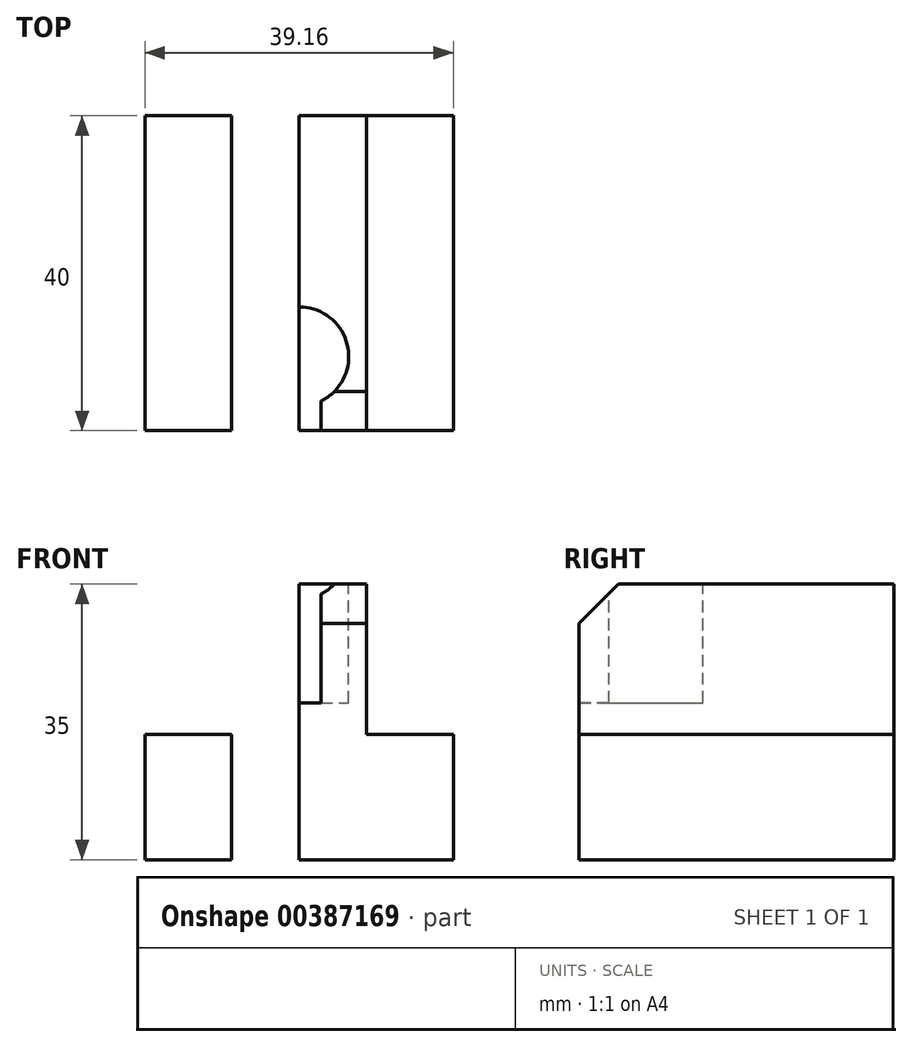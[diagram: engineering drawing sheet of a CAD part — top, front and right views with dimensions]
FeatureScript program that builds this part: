
annotation { "Feature Type Name" : "Feature", "Feature Type Description" : "" }
export const myFeature = defineFeature(function(context is Context, id is Id, definition is map)
    precondition{}
    {
        {
            var Q0;
            Q0=qCreatedBy(makeId("Front.planeOp"),FACE);
            var sketch = newSketch(context, id + "F0", { "sketchPlane" : qUnion([Q0])});
            skLineSegment(sketch, "E0", {"start": v(0, 0) * mm, "end": v(19.58, 0) * mm});
            skLineSegment(sketch, "E1", {"start": v(0, 0) * mm, "end": v(-19.58, 0) * mm});
            skLineSegment(sketch, "E2", {"start": v(0, 0) * mm, "end": v(0, 35) * mm});
            skLineSegment(sketch, "E3", {"start": v(19.58, 0) * mm, "end": v(8.59, 0) * mm});
            skLineSegment(sketch, "E4.MirrorCS", {"start": v(-19.58, 0) * mm, "end": v(-8.59, 0) * mm});
            skLineSegment(sketch, "E5", {"start": v(8.59, 0) * mm, "end": v(8.59, 35) * mm});
            skLineSegment(sketch, "E6", {"start": v(8.59, 35) * mm, "end": v(0, 35) * mm});
            skLineSegment(sketch, "E7.MirrorCS", {"start": v(-8.59, 35) * mm, "end": v(0, 35) * mm});
            skLineSegment(sketch, "E8.MirrorCS", {"start": v(-8.59, 0) * mm, "end": v(-8.59, 35) * mm});
            skLineSegment(sketch, "E9", {"start": v(0, 35) * mm, "end": v(0, 19.94) * mm});
            skLineSegment(sketch, "E10", {"start": v(0, 19.94) * mm, "end": v(0, 15.94) * mm});
            skLineSegment(sketch, "E11", {"start": v(0, 15.94) * mm, "end": v(8.59, 15.94) * mm});
            skLineSegment(sketch, "E12", {"start": v(8.59, 15.94) * mm, "end": v(19.58, 15.94) * mm});
            skLineSegment(sketch, "E13", {"start": v(19.58, 15.94) * mm, "end": v(19.58, 0) * mm});
            skLineSegment(sketch, "E14.MirrorCS", {"start": v(-8.59, 15.94) * mm, "end": v(-19.58, 15.94) * mm});
            skLineSegment(sketch, "E15.MirrorCS", {"start": v(-19.58, 15.94) * mm, "end": v(-19.58, 0) * mm});
            skSolve(sketch);
        }
        {
            var Q0;
            {var subQ0=sQuery(id+"F0.wireOp",EDGE,"E4.MirrorCS");Q0=makeQuery(id+"F0.imprint","IMPRINT",FACE,{"disambiguationData":[TD([[makeQuery(id+"F0.imprint","IMPRINT",EDGE,{"derivedFrom":subQ0}),1.0]])]});}
            var Q1;
            {var subQ1=sQuery(id+"F0.wireOp",EDGE,"E1");Q1=makeQuery(id+"F0.imprint","IMPRINT",FACE,{"disambiguationData":[TD([[makeQuery(id+"F0.imprint","IMPRINT",EDGE,{"derivedFrom":subQ1}),-1.0]])]});}
            var Q2;
            {var subQ0=sQuery(id+"F0.wireOp",EDGE,"E0");Q2=makeQuery(id+"F0.imprint","IMPRINT",FACE,{"disambiguationData":[TD([[makeQuery(id+"F0.imprint","IMPRINT",EDGE,{"derivedFrom":subQ0}),1.0]])]});}
            var Q3;
            {var subQ0=sQuery(id+"F0.wireOp",EDGE,"E3");Q3=makeQuery(id+"F0.imprint","IMPRINT",FACE,{"disambiguationData":[TD([[makeQuery(id+"F0.imprint","IMPRINT",EDGE,{"derivedFrom":subQ0}),-1.0]])]});}
            var Q4;
            {var subQ0=sQuery(id+"F0.wireOp",EDGE,"E6");Q4=makeQuery(id+"F0.imprint","IMPRINT",FACE,{"disambiguationData":[TD([[makeQuery(id+"F0.imprint","IMPRINT",EDGE,{"derivedFrom":subQ0}),1.0]])]});}
            extrude(context, id + "F1", {"entities" : qUnion([Q0, Q1, Q2, Q3, Q4]), "depth" : 40 * mm});
        }
        {
            var Q0;
            Q0=makeQuery(id+"F1.opExtrude","CAP_EDGE",EDGE,{"disambiguationData":[OSD([sQuery(id+"F0.wireOp",EDGE,"E6"),sQuery(id+"F0.wireOp",EDGE,"E7.MirrorCS")])],"isStart":false});
            chamfer(context, id + "F2", {"entities" : qUnion([Q0]), "width" : 5 * mm, "tangentPropagation" : true});
        }
        {
            var Q0;
            Q0=makeQuery(id+"F1.opExtrude","SWEPT_FACE",FACE,{"disambiguationData":[OSD([sQuery(id+"F0.wireOp",EDGE,"E8.MirrorCS")])]});
            var sketch = newSketch(context, id + "F3", { "sketchPlane" : qUnion([Q0])});
            skCircle(sketch, "E16", {"center": v(30.87, 29.64) * mm, "radius": 2.5 * mm});
            skSolve(sketch);
        }
        {
            var Q0;
            Q0=makeQuery(id+"F3.imprint","IMPRINT",FACE,{"disambiguationData":[TD([[makeQuery(id+"F3.imprint","IMPRINT",EDGE,{"derivedFrom":sQuery(id+"F3.wireOp",EDGE,"E16")}),1.0]])]});
            extrude(context, id + "F4", {"entities" : qUnion([Q0]), "operationType" : NewBodyOperationType.REMOVE, "oppositeDirection" : true, "depth" : 25.4 * mm});
        }
        {
            var Q0;
            Q0=makeQuery(id+"F1.opExtrude","SWEPT_FACE",FACE,{"disambiguationData":[OSD([sQuery(id+"F0.wireOp",EDGE,"E6"),sQuery(id+"F0.wireOp",EDGE,"E7.MirrorCS")])]});
            var sketch = newSketch(context, id + "F5", { "sketchPlane" : qUnion([Q0])});
            skCircle(sketch, "E17", {"center": v(0, -30.58) * mm, "radius": 6.3 * mm});
            skLineSegment(sketch, "E18", {"start": v(0, -35) * mm, "end": v(2.77, -35) * mm});
            skLineSegment(sketch, "E19.MirrorCS", {"start": v(0, -35) * mm, "end": v(-2.77, -35) * mm});
            skLineSegment(sketch, "E20", {"start": v(-2.77, -35) * mm, "end": v(-2.77, -40) * mm});
            skLineSegment(sketch, "E21.MirrorCS", {"start": v(2.77, -35) * mm, "end": v(2.77, -40) * mm});
            skLineSegment(sketch, "E22", {"start": v(2.77, -40) * mm, "end": v(-2.77, -40) * mm});
            skSolve(sketch);
        }
        {
            var Q0;
            {var subQ0=sQuery(id+"F5.wireOp",EDGE,"E18");Q0=makeQuery(id+"F5.imprint","IMPRINT",FACE,{"disambiguationData":[TD([[makeQuery(id+"F5.imprint","IMPRINT",EDGE,{"derivedFrom":subQ0}),1.0]])]});}
            var Q1;
            {var subQ1=sQuery(id+"F5.wireOp",EDGE,"E18");Q1=makeQuery(id+"F5.imprint","IMPRINT",FACE,{"disambiguationData":[TD([[makeQuery(id+"F5.imprint","IMPRINT",EDGE,{"derivedFrom":subQ1}),-1.0]])]});}
            var Q2;
            {var subQ0=sQuery(id+"F5.wireOp",EDGE,"E21.MirrorCS");var subQ1=sQuery(id+"F5.wireOp",EDGE,"E17");var subQ2=makeQuery(id+"F5.imprint","INTERSECT",VERTEX,{"derivedFrom":[subQ1,subQ0]});Q2=makeQuery(id+"F5.imprint","IMPRINT",FACE,{"disambiguationData":[TD([[makeQuery(id+"F5.imprint","IMPRINT",EDGE,{"disambiguationData":[TD([[subQ2,-1.0]])],"derivedFrom":subQ1}),1.0]])]});}
            var Q3;
            {var subQ5=sQuery(id+"F5.wireOp",EDGE,"E22");Q3=makeQuery(id+"F5.imprint","IMPRINT",FACE,{"disambiguationData":[TD([[makeQuery(id+"F5.imprint","IMPRINT",EDGE,{"derivedFrom":subQ5}),-1.0]])]});}
            var Q4;
            {var subQ0=sQuery(id+"F5.wireOp",EDGE,"E20");var subQ1=sQuery(id+"F5.wireOp",EDGE,"E17");var subQ2=makeQuery(id+"F5.imprint","INTERSECT",VERTEX,{"derivedFrom":[subQ1,subQ0]});Q4=makeQuery(id+"F5.imprint","IMPRINT",FACE,{"disambiguationData":[TD([[makeQuery(id+"F5.imprint","IMPRINT",EDGE,{"disambiguationData":[TD([[subQ2,1.0]])],"derivedFrom":subQ1}),1.0]])]});}
            extrude(context, id + "F6", {"entities" : qUnion([Q0, Q1, Q2, Q3, Q4]), "operationType" : NewBodyOperationType.REMOVE, "oppositeDirection" : true, "depth" : 15.06 * mm});
        }
    });
